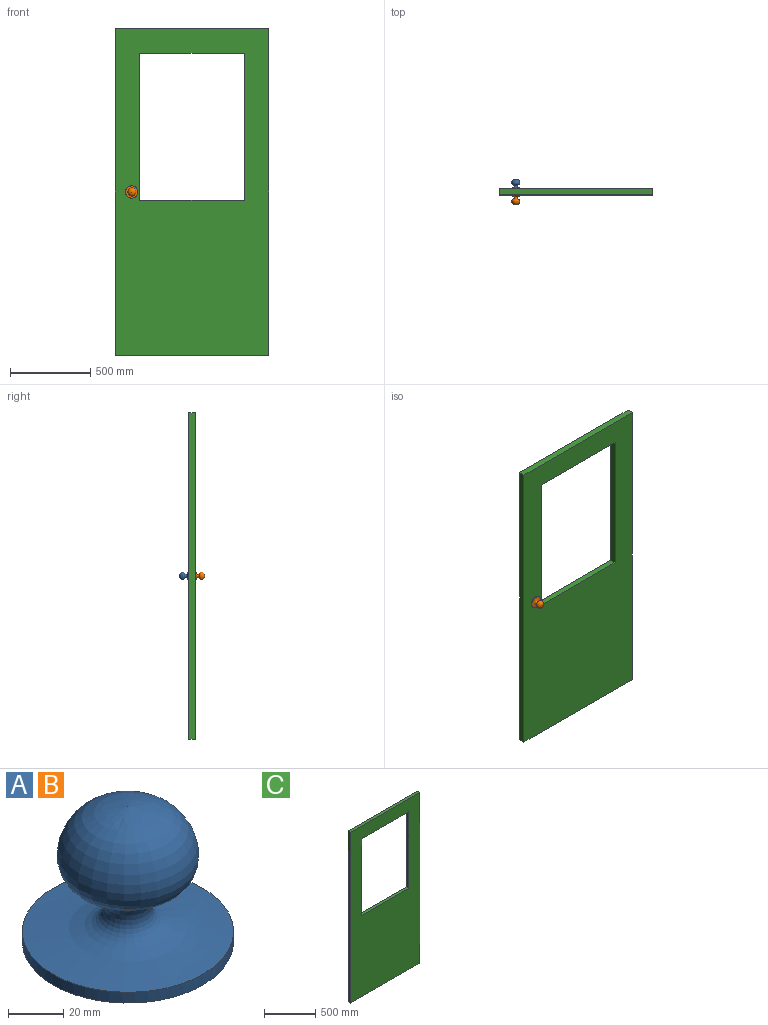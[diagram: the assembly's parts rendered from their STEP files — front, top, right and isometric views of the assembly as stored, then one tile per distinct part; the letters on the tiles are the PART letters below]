
ASSEMBLY  parts=3 mates=2
PART A: 3 faces, bbox 76.2x76.2x59.7 mm
  f0: plane 76.2x76.2mm, normal (0,0,-1), area 4560.4mm2, adj f1
  f1: cylinder r=38.1mm len=76.2mm, axis (0,0,-1), area 1144.1mm2, adj f0,f2
  f2: revolved ~76.2x76.2mm, area 11612.3mm2, adj f1
PART B: same geometry as A
PART C: 10 faces, bbox 952.5x38.1x2032 mm
  f0: plane 2032x952.5mm, normal (0,-1,0), area 1343223.1mm2, adj f2,f3,f4,f5,f6,f7,f8,f9
  f1: plane 2032x952.5mm, normal (0,1,0), area 1343223.1mm2, adj f2,f3,f4,f5,f6,f7,f8,f9
  f2: plane 952.5x38.1mm, normal (0,0,-1), area 36290.2mm2, adj f0,f1,f3,f5
  f3: plane 2032x38.1mm, normal (1,0,0), area 77419.2mm2, adj f0,f1,f2,f4
  f4: plane 952.5x38.1mm, normal (0,0,1), area 36290.2mm2, adj f0,f1,f3,f5
  f5: plane 2032x38.1mm, normal (-1,0,0), area 77419.2mm2, adj f0,f1,f2,f4
  f6: plane 647.7x38.1mm, normal (0,0,-1), area 24677.4mm2, adj f0,f1,f7,f9
  f7: plane 914.4x38.1mm, normal (1,0,0), area 34838.6mm2, adj f0,f1,f6,f8
  f8: plane 647.7x38.1mm, normal (0,0,1), area 24677.4mm2, adj f0,f1,f7,f9
  f9: plane 914.4x38.1mm, normal (-1,0,0), area 34838.6mm2, adj f0,f1,f6,f8
PLACE A rot(axis=(-1,0,0),90deg) t=(-850.9,8.63,1016)mm
PLACE B rot(axis=(1,0,0),90deg) t=(-850.9,-46.73,1016)mm
PLACE C t=(-476.25,-19.05,1016)mm
MATE fastened A.f1 <-> C.f1  axis (0,-1,0) through (-850.9,0,1016)mm
MATE fastened B.f1 <-> C.f0  axis (0,1,0) through (-850.9,-38.1,1016)mm
